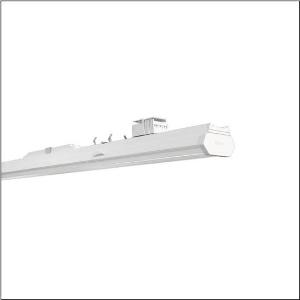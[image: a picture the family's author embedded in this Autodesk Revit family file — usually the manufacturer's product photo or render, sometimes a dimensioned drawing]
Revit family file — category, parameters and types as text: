
# Revit family: licross_r__11_protected_ho_51td11cn4exs_ee6c
name_source: partatom
category: Lighting Fixtures
units: mm (PartAtom-declared; Revit-internal decimal feet)

## family parameters
Cut with Voids When Loaded = No
Host = Face
Light Source = No
Part Type = Normal
Room Calculation Point = No
Round Connector Dimension = Use Diameter
Shared = No

## types (1)
- --- (1 x LED, 14460 lm, 77.6 W, 4000K)
    Apparent Load = 78 VA
    CIE Flux Codes = 84 94 98 99 100
    Color Rendering = 80
    Color Temperature = 4000K
    Default Elevation = 1800 mm
    Description = Licross® 11 Protected HO, luminaire insert, of sheet steel, galvanised, coil coated, white, length: 1.500mm, width: 90mm, height: 101mm, LED rated luminous flux: 14.460lm, light colour: 840, control gear: ON/OFF Multilumen, CLOi, with plug, 3-pole, with phase selection, mains connection: 220..240V, AC, 50/60Hz, start of lifetime: 78W, end of service life: 87W, halogen-free wiring, primary light control with lens, of plastic, primary optical cover: cover, of PMMA, light emission: direct distribution, primary light characteristic: symmetric, protection rating (complete): IP54, insulation class (complete): insulation class I (protective earthing), certification: CE, ENEC, VDE, UKCA, protection symbol: D if used in an environment with non-conductive dust loads with corresponding accessories, impact resistance: IK06, permissible ambient temperature for indoor applications: -35..+35°C, corresponds to IFS (International Featured Standards) requirements for safety and quality in the food industry, reducing of maximum allowable ambient temperature of 5°C with ceiling mounting, LABS conformity tested according to VDMA 24364:2018-05, packaging unit: 1 piece
    Height = 92 mm
    Lamp = 1 x LED
    Lamp Light Flux = 14460 lm
    Lamp Power = 77.6 W
    Lamp count = 1
    Length = 1500 mm
    Luminous efficacy = 186 lm/W
    Manufacturer = Siteco
    ModVariant = No
    Model = 51TD11CN4EXS
    Mounting Place = Ceiling
    Mounting Type = Pendant
    Number of Poles = 1
    OnlyDefault = Yes
    Power Factor = 1
    Product Name = Licross® 11 Protected HO
    Product group = luminaire insert
    ProductGroupID = 901
    Protection Class = Protection class I
    Protection Degree = IP 54
    RLX_Detail_Level = 1
    RLX_Emergency_Light_Flux = 0 lm
    RLX_Emergency_Type = 0
    RLX_Emergency_Type_DB = No
    RlxData = <blob elided: 22133 chars, md5=23ed408f>
    Socket = socket
    Standby Power = 0 W
    System Light Flux = 14460 lm
    System Power = 78 W
    Type Comments = factory setting: luminous flux: 100 % | (A | C | E) | 181 mA
    Type Image = l_1256145.jpg
    URL = http://relux.com
    VarID = @adj_019347
    Voltage = 0 V
    Weight = 0.00 kg
    Width = 88 mm

## geometry (parser evidence)
native form markers: Blend x4, Sweep x9
no freeform markers — native parametric forms only
